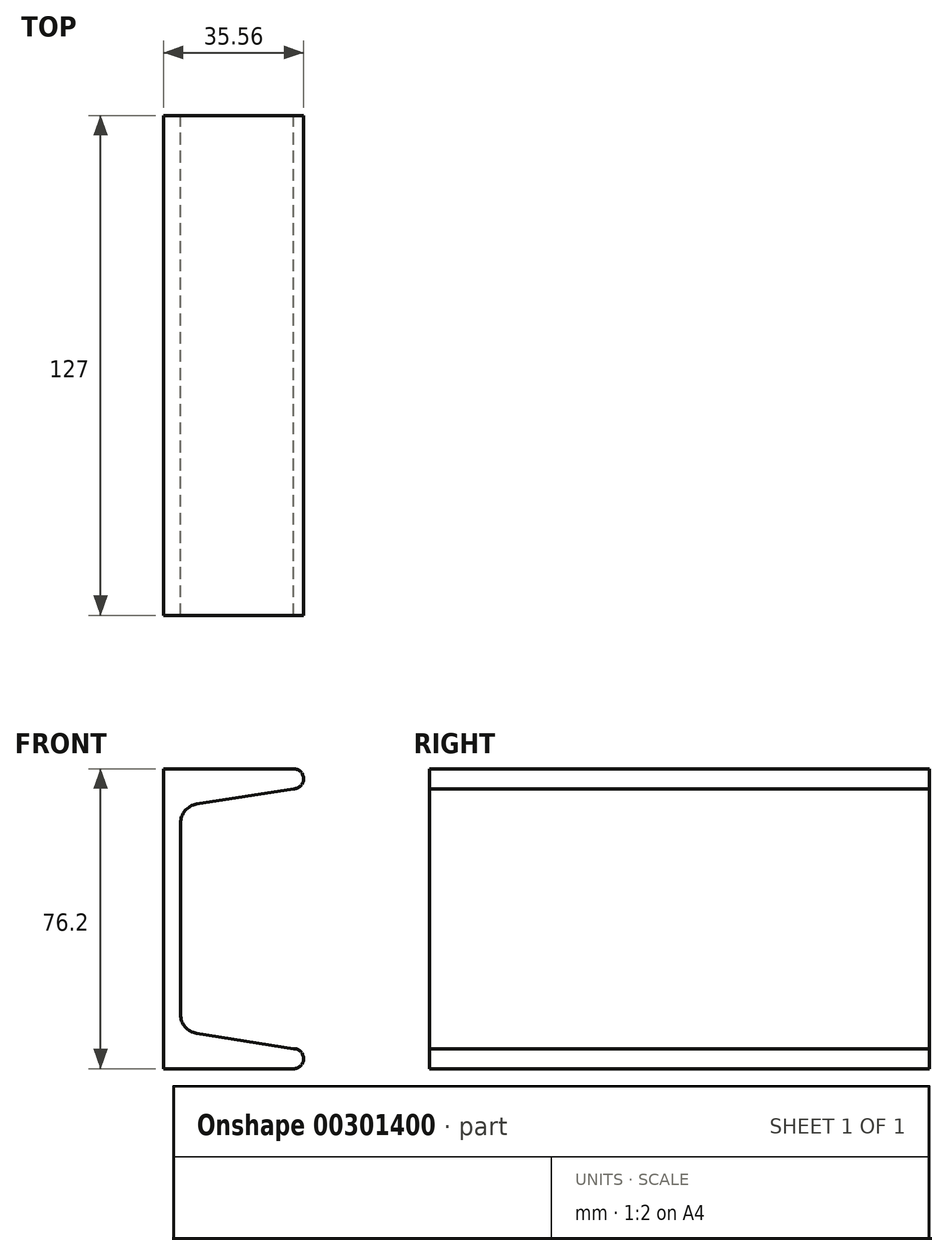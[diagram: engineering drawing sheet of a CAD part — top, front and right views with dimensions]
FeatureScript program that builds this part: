
annotation { "Feature Type Name" : "Feature", "Feature Type Description" : "" }
export const myFeature = defineFeature(function(context is Context, id is Id, definition is map)
    precondition{}
    {
        {
            var Q0;
            Q0=qCreatedBy(makeId("Front.planeOp"),FACE);
            var sketch = newSketch(context, id + "F0", { "sketchPlane" : qUnion([Q0])});
            skLineSegment(sketch, "E0", {"start": v(0, 0) * mm, "end": v(0, 76.2) * mm});
            skLineSegment(sketch, "E1", {"start": v(0, 76.2) * mm, "end": v(65.1, 76.2) * mm});
            skLineSegment(sketch, "E2", {"start": v(0, 0) * mm, "end": v(33.02, 0) * mm});
            skLineSegment(sketch, "E3", {"start": v(0, 36.28) * mm, "end": v(4.32, 36.28) * mm});
            skLineSegment(sketch, "E4", {"start": v(0, 76.2) * mm, "end": v(4.32, 76.2) * mm});
            skLineSegment(sketch, "E5", {"start": v(4.32, 62.43) * mm, "end": v(4.32, 13.77) * mm});
            skLineSegment(sketch, "E6", {"start": v(0, 0) * mm, "end": v(65.1, 0) * mm});
            skLineSegment(sketch, "E7", {"start": v(65.1, 0) * mm, "end": v(8.41, 8.98) * mm});
            skLineSegment(sketch, "E8", {"start": v(65.1, 76.2) * mm, "end": v(8.41, 67.22) * mm});
            skArc(sketch, "E9", {"start": v(33.02, 0) * mm, "mid": v(35.56, 2.54) * mm, "end": v(33.02, 5.08) * mm});
            skLineSegment(sketch, "E10", {"start": v(0, 76.2) * mm, "end": v(33.02, 76.2) * mm});
            skArc(sketch, "E11", {"start": v(33.02, 71.12) * mm, "mid": v(35.56, 73.66) * mm, "end": v(33.02, 76.2) * mm});
            skArc(sketch, "E12.filletArc", {"start": v(4.32, 13.77) * mm, "mid": v(5.48, 10.62) * mm, "end": v(8.41, 8.98) * mm});
            skArc(sketch, "E13.filletArc", {"start": v(8.41, 67.22) * mm, "mid": v(5.48, 65.58) * mm, "end": v(4.32, 62.43) * mm});
            skSolve(sketch);
        }
        {
            var Q0;
            {var subQ0=sQuery(id+"F0.wireOp",EDGE,"E9");var subQ1=sQuery(id+"F0.wireOp",EDGE,"E7");var subQ2=makeQuery(id+"F0.imprint","INTERSECT",VERTEX,{"disambiguationData":[OD(0.0)],"derivedFrom":[subQ1,subQ0]});Q0=makeQuery(id+"F0.imprint","IMPRINT",FACE,{"disambiguationData":[TD([[makeQuery(id+"F0.imprint","IMPRINT",EDGE,{"disambiguationData":[TD([[subQ2,1.0]])],"derivedFrom":subQ1}),-1.0]])]});}
            var Q1;
            {var subQ0=sQuery(id+"F0.wireOp",EDGE,"E11");var subQ1=sQuery(id+"F0.wireOp",EDGE,"E8");var subQ2=makeQuery(id+"F0.imprint","INTERSECT",VERTEX,{"disambiguationData":[OD(0.0)],"derivedFrom":[subQ1,subQ0]});Q1=makeQuery(id+"F0.imprint","IMPRINT",FACE,{"disambiguationData":[TD([[makeQuery(id+"F0.imprint","IMPRINT",EDGE,{"disambiguationData":[TD([[subQ2,1.0]])],"derivedFrom":subQ1}),1.0]])]});}
            var Q2;
            {var subQ5=sQuery(id+"F0.wireOp",EDGE,"E3");Q2=makeQuery(id+"F0.imprint","IMPRINT",FACE,{"disambiguationData":[TD([[makeQuery(id+"F0.imprint","IMPRINT",EDGE,{"derivedFrom":subQ5}),-1.0]])]});}
            var Q3;
            {var subQ7=sQuery(id+"F0.wireOp",EDGE,"E3");Q3=makeQuery(id+"F0.imprint","IMPRINT",FACE,{"disambiguationData":[TD([[makeQuery(id+"F0.imprint","IMPRINT",EDGE,{"derivedFrom":subQ7}),1.0]])]});}
            extrude(context, id + "F1", {"entities" : qUnion([Q0, Q1, Q2, Q3]), "depth" : 127 * mm});
        }
    });
